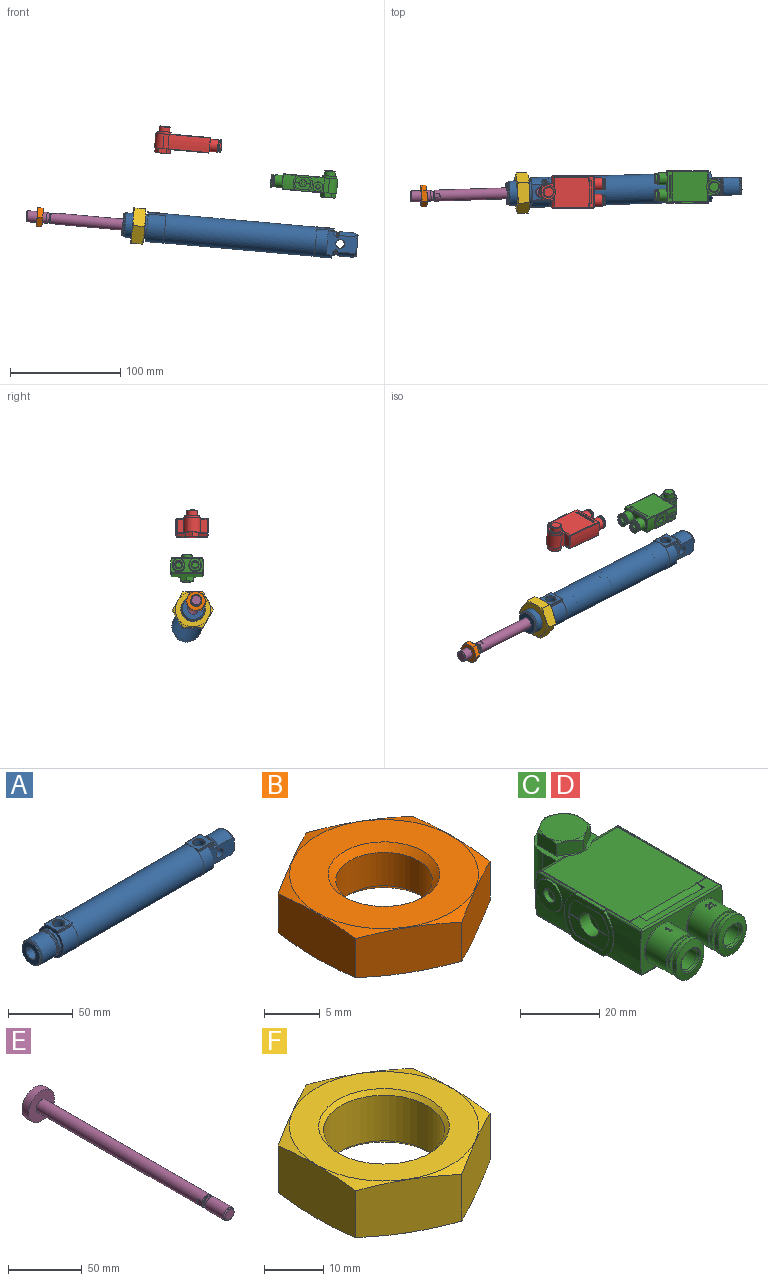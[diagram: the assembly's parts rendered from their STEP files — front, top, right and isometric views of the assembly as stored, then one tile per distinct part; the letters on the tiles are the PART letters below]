
ASSEMBLY  parts=6 mates=5
PART A: 96 faces, bbox 213.8x27.3x27.3 mm
  f0: cone r=866.03mm half-angle=60deg, axis (0,0,1), area 66.5mm2, adj f1
  f1: cylinder r=4.28mm len=21.42mm, axis (0,0,-1), area 576.4mm2, adj f0,f56
  f2: cone r=4.28mm half-angle=45deg, axis (0,0,1), area 23.6mm2, adj f3,f34
  f3: cylinder r=4.28mm len=10.34mm, axis (0,0,-1), area 278.2mm2, adj f2,f55
  f4: cylinder r=13.5mm len=27mm, axis (1,0,0), area 804.5mm2, adj f7,f21,f25,f52,f53,f66,f67,f68
  f5: cylinder r=4.28mm len=8.57mm, axis (0,0,-1), area 172.8mm2, adj f6,f55
  f6: plane 8.57x8.57mm, normal (0,0,1), area 57.6mm2, adj f5
  f7: plane 27.79x22.04mm, normal (0,-1,0), area 388.5mm2, adj f4,f8,f9,f10,f11,f12,f13,f60
  f8: torus R=10.65mm, axis (1,0,0), area 11.6mm2, adj f7,f67,f86,f88
  f9: torus R=10.65mm, axis (1,0,0), area 22.9mm2, adj f7,f67,f86,f91
  f10: cone r=11mm half-angle=45deg, axis (-1,0,0), area 25.8mm2, adj f7,f11,f64,f67
  f11: cylinder r=11mm len=16mm, axis (-1,0,0), area 267.8mm2, adj f7,f10,f67,f88
  f12: cylinder r=11mm len=16mm, axis (-1,0,0), area 267.8mm2, adj f7,f13,f65,f67
  f13: cone r=10.08mm half-angle=45deg, axis (1,0,0), area 23.6mm2, adj f7,f12,f67,f89
  f14: plane 3.86x0.71mm, normal (-1,0,0), area 2.5mm2, adj f16,f17,f69,f75
  f15: plane 3.86x0.71mm, normal (1,0,0), area 2.5mm2, adj f18,f20,f69,f75
  f16: plane 3.04x1.25mm, normal (0,0,1), area 2.8mm2, adj f14,f17
  f17: cone r=1.95mm half-angle=45deg, axis (0,0,-1), area 2.8mm2, adj f14,f16,f75
  f18: plane 3.04x1.25mm, normal (0,0,1), area 2.8mm2, adj f15,f20
  f19: cylinder r=0.4mm len=2.71mm, axis (1,0,0), area 1.5mm2, adj f21,f22,f49,f73
  f20: cone r=1.95mm half-angle=45deg, axis (0,0,-1), area 2.8mm2, adj f15,f18,f75
  f21: cylinder r=2.5mm len=6.7mm, axis (0,0,1), area 51.7mm2, adj f4,f19,f22,f49,f50,f51,f52,f53
  f22: plane 16x13.7mm, normal (0,0,1), area 144.5mm2, adj f19,f21,f23,f51,f56,f73,f94
  f23: cylinder r=0.4mm len=16mm, axis (1,0,0), area 10.1mm2, adj f22,f24,f73,f94
  f24: plane 16x1.55mm, normal (0,-1,0), area 24.8mm2, adj f23,f25,f73,f94
  f25: cylinder r=0.3mm len=16mm, axis (1,0,0), area 4.8mm2, adj f4,f24,f73,f94
  f26: cylinder r=13.25mm len=137.5mm, axis (-1,0,0), area 11447.2mm2, adj f73,f76
  f27: plane 3.9x0.6mm, normal (0,0,1), area 2.3mm2, adj f28,f30,f72
  f28: plane 3.86x0.71mm, normal (-1,0,0), area 2.5mm2, adj f27,f29,f30,f71
  f29: cone r=1.95mm half-angle=45deg, axis (0,0,-1), area 2.8mm2, adj f28,f30,f71
  f30: cylinder r=1.95mm len=3.9mm, axis (0,0,1), area 4mm2, adj f27,f28,f29,f31,f54,f72
  f31: plane 5x5mm, normal (0,0,1), area 7.7mm2, adj f30,f32
  f32: cylinder r=2.5mm len=6.7mm, axis (0,0,1), area 51.7mm2, adj f31,f33,f34,f78,f79,f80,f81,f82
  f33: cylinder r=0.4mm len=10.91mm, axis (1,0,0), area 6.7mm2, adj f32,f34,f77,f82
  f34: plane 16x13.7mm, normal (0,0,1), area 144.5mm2, adj f2,f32,f33,f35,f76,f77,f83
  f35: cylinder r=0.4mm len=16mm, axis (1,0,0), area 10.1mm2, adj f34,f36,f76,f77
  f36: plane 16x1.55mm, normal (0,-1,0), area 24.8mm2, adj f35,f37,f76,f77
  f37: cylinder r=0.3mm len=16mm, axis (1,0,0), area 4.8mm2, adj f36,f76,f77,f78
  f38: cylinder r=11mm len=22mm, axis (-1,0,0), area 138.2mm2, adj f39,f77
  f39: plane 22x22mm, normal (-1,0,0), area 23.8mm2, adj f38,f40
  f40: torus R=10.65mm, axis (1,0,0), area 80.1mm2, adj f39,f41
  f41: cylinder r=9.85mm len=19.7mm, axis (-1,0,0), area 47.6mm2, adj f40,f42
  f42: torus R=10.65mm, axis (1,0,0), area 39.2mm2, adj f41,f43
  f43: cone r=11mm half-angle=45deg, axis (-1,0,0), area 85.8mm2, adj f42,f44
  f44: cylinder r=11mm len=22mm, axis (-1,0,0), area 1033.3mm2, adj f43,f45
  f45: cone r=10mm half-angle=45deg, axis (1,0,0), area 93.3mm2, adj f44,f46
  f46: cylinder r=10mm len=20mm, axis (-1,0,0), area 50.3mm2, adj f45,f47
  f47: cone r=9.8mm half-angle=45deg, axis (1,0,0), area 17.6mm2, adj f46,f48
  f48: plane 19.6x19.6mm, normal (-1,0,0), area 223.2mm2, adj f47,f55
  f49: plane 2.12x1.55mm, normal (0,1,0), area 3.3mm2, adj f19,f21,f52,f73
  f50: plane 10.52x1.55mm, normal (0,1,0), area 16.3mm2, adj f21,f51,f53,f94
  f51: cylinder r=0.4mm len=11.11mm, axis (1,0,0), area 6.8mm2, adj f21,f22,f50,f94
  f52: cylinder r=0.3mm len=2.12mm, axis (1,0,0), area 0.6mm2, adj f4,f21,f49,f73
  f53: cylinder r=0.3mm len=10.52mm, axis (1,0,0), area 3.1mm2, adj f4,f21,f50,f94
  f54: cone r=1.95mm half-angle=45deg, axis (0,0,-1), area 2.8mm2, adj f30,f70,f72
  f55: cylinder r=5mm len=52.6mm, axis (-1,0,0), area 1522.1mm2, adj f3,f5,f48,f59
  f56: cone r=4.28mm half-angle=45deg, axis (0,0,1), area 23.6mm2, adj f1,f22
  f57: plane 25x25mm, normal (-1,0,0), area 490.9mm2, adj f58
  f58: cylinder r=12.5mm len=106.25mm, axis (-1,0,0), area 8344.9mm2, adj f57,f59
  f59: plane 25x25mm, normal (1,0,0), area 412.3mm2, adj f55,f58
  f60: cone r=10mm half-angle=45deg, axis (-1,0,0), area 5.3mm2, adj f7,f61,f63,f67
  f61: plane 19.6x16mm, normal (1,0,0), area 274mm2, adj f7,f60,f62,f67
  f62: cone r=10mm half-angle=45deg, axis (-1,0,0), area 5.3mm2, adj f7,f61,f64,f67
  f63: cylinder r=10mm len=16mm, axis (-1,0,0), area 14.8mm2, adj f7,f60,f65,f67
  f64: cylinder r=10mm len=16mm, axis (-1,0,0), area 14.8mm2, adj f7,f10,f62,f67
  f65: cone r=11mm half-angle=45deg, axis (-1,0,0), area 25.8mm2, adj f7,f12,f63,f67
  f66: plane 21.75x5.5mm, normal (1,0,0), area 83.7mm2, adj f4,f67
  f67: plane 27.79x22.04mm, normal (0,1,0), area 388.5mm2, adj f4,f8,f9,f10,f11,f12,f13,f60
  f68: plane 21.75x5.5mm, normal (1,0,0), area 83.7mm2, adj f4,f7
  f69: plane 3.9x0.6mm, normal (0,0,1), area 2.3mm2, adj f14,f15,f75
  f70: plane 3.04x1.25mm, normal (0,0,1), area 2.8mm2, adj f54,f72
  f71: plane 3.04x1.25mm, normal (0,0,1), area 2.8mm2, adj f28,f29
  f72: plane 3.86x0.71mm, normal (1,0,0), area 2.5mm2, adj f27,f30,f54,f70
  f73: plane 27x27mm, normal (-1,0,0), area 30.8mm2, adj f4,f19,f22,f23,f24,f25,f26,f49
  f74: plane 5x5mm, normal (0,0,1), area 7.7mm2, adj f21,f75
  f75: cylinder r=1.95mm len=3.9mm, axis (0,0,1), area 4mm2, adj f14,f15,f17,f20,f69,f74
  f76: plane 27x27mm, normal (1,0,0), area 30.8mm2, adj f26,f34,f35,f36,f37,f78,f80,f81
  f77: plane 27x27mm, normal (-1,0,0), area 202.2mm2, adj f33,f34,f35,f36,f37,f38,f78,f79
  f78: cylinder r=13.5mm len=27mm, axis (1,0,0), area 1082.7mm2, adj f32,f37,f76,f77,f79,f80
  f79: cylinder r=0.3mm len=10.32mm, axis (1,0,0), area 3mm2, adj f32,f77,f78,f82
  f80: cylinder r=0.3mm len=2.32mm, axis (1,0,0), area 0.7mm2, adj f32,f76,f78,f81
  f81: plane 2.32x1.55mm, normal (0,1,0), area 3.6mm2, adj f32,f76,f80,f83
  f82: plane 10.32x1.55mm, normal (0,1,0), area 16mm2, adj f32,f33,f77,f79
  f83: cylinder r=0.4mm len=2.91mm, axis (1,0,0), area 1.6mm2, adj f32,f34,f76,f81
  f84: cylinder r=4mm len=16mm, axis (0,-1,0), area 402.1mm2, adj f7,f67
  f85: torus R=10.65mm, axis (1,0,0), area 22.9mm2, adj f7,f67,f87,f90
  f86: cylinder r=9.85mm len=16mm, axis (-1,0,0), area 14.4mm2, adj f7,f8,f9,f67
  f87: cylinder r=9.85mm len=16mm, axis (-1,0,0), area 14.4mm2, adj f7,f67,f85,f89
  f88: cone r=10.08mm half-angle=45deg, axis (1,0,0), area 23.6mm2, adj f7,f8,f11,f67
  f89: torus R=10.65mm, axis (1,0,0), area 11.6mm2, adj f7,f13,f67,f87
  f90: plane 16x3.97mm, normal (1,0,0), area 6.3mm2, adj f7,f67,f85,f92
  f91: plane 16x3.97mm, normal (1,0,0), area 6.3mm2, adj f7,f9,f67,f93
  f92: cylinder r=11mm len=16mm, axis (-1,0,0), area 35.8mm2, adj f7,f67,f90,f94
  f93: cylinder r=11mm len=16mm, axis (-1,0,0), area 35.8mm2, adj f7,f67,f91,f95
  f94: plane 16x5.95mm, normal (1,0,0), area 53.5mm2, adj f4,f7,f22,f23,f24,f25,f50,f51
  f95: plane 16x5.95mm, normal (1,0,0), area 43.7mm2, adj f4,f7,f67,f93
PART B: 13 faces, bbox 19.6x19.6x5 mm
  f0: plane 9.82x4.98mm, normal (-1,0,0), area 46.4mm2, adj f1,f2,f4,f8
  f1: plane 8.5x4.98mm, normal (-0.5,0.87,0), area 46.4mm2, adj f0,f2,f8,f12
  f2: cone r=17.78mm half-angle=75deg, axis (0,0,1), area 26.9mm2, adj f0,f1,f3,f4,f5,f6,f12
  f3: plane 9.82x4.98mm, normal (1,0,0), area 46.4mm2, adj f2,f6,f8,f12
  f4: plane 8.5x4.98mm, normal (-0.5,-0.87,0), area 46.4mm2, adj f0,f2,f6,f8
  f5: plane 16.9x16.9mm, normal (0,0,-1), area 145.8mm2, adj f2,f9
  f6: plane 8.5x4.98mm, normal (0.5,-0.87,0), area 46.4mm2, adj f2,f3,f4,f8
  f7: plane 16.9x16.9mm, normal (0,0,1), area 145.8mm2, adj f8,f11
  f8: cone r=8.45mm half-angle=75deg, axis (0,0,-1), area 26.9mm2, adj f0,f1,f3,f4,f6,f7,f12
  f9: cone r=4.32mm half-angle=45deg, axis (0,0,-1), area 28mm2, adj f5,f10
  f10: cylinder r=4.32mm len=8.65mm, axis (0,0,1), area 99.1mm2, adj f9,f11
  f11: cone r=5mm half-angle=45deg, axis (0,0,1), area 28mm2, adj f7,f10
  f12: plane 8.5x4.98mm, normal (0.5,0.87,0), area 46.4mm2, adj f1,f2,f3,f8
PART C: 172 faces, bbox 30.2x60.9x25 mm
  f0: cylinder r=3.3mm len=6.6mm, axis (1,0,0), area 71.5mm2, adj f64,f137,f138,f139,f169
  f1: cylinder r=4.5mm len=9mm, axis (-1,0,0), area 8.7mm2, adj f2,f117
  f2: plane 9x9mm, normal (-1,0,0), area 51.7mm2, adj f1,f3
  f3: cylinder r=1.95mm len=3.9mm, axis (1,0,0), area 18.4mm2, adj f2,f4
  f4: plane 3.9x3.9mm, normal (-1,0,0), area 11.9mm2, adj f3
  f5: plane 0.52x0.28mm, normal (0,-1,0), area 0.1mm2, adj f6,f15,f16,f63
  f6: plane 0.51x0.24mm, normal (1,0,0), area 0.1mm2, adj f5,f7,f16,f63
  f7: plane 0.8x0.53mm, normal (0,1,0), area 0.4mm2, adj f6,f8,f16,f63
  f8: plane 0.51x0.24mm, normal (-1,0,0), area 0.1mm2, adj f7,f9,f16,f63
  f9: plane 0.52x0.28mm, normal (0,-1,0), area 0.1mm2, adj f8,f10,f16,f63
  f10: plane 1.68x0.52mm, normal (-1,0,0), area 0.9mm2, adj f9,f11,f16,f63
  f11: plane 0.53x0.24mm, normal (0,-1,0), area 0.1mm2, adj f10,f12,f16,f63
  f12: plane 0.52x0.4mm, normal (0.82,-0.57,0), area 0.3mm2, adj f11,f13,f16,f63
  f13: plane 0.51x0.34mm, normal (1,0,0), area 0.2mm2, adj f12,f14,f16,f63
  f14: plane 0.52x0.4mm, normal (-0.82,0.57,0), area 0.3mm2, adj f13,f15,f16,f63
  f15: plane 1.34x0.52mm, normal (1,0,0), area 0.7mm2, adj f5,f14,f16,f63
  f16: plane 1.92x0.8mm, normal (0,0,1), area 0.7mm2, adj f5,f6,f7,f8,f9,f10,f11,f12
  f17: plane 0.52x0.28mm, normal (0,-1,0), area 0.1mm2, adj f18,f27,f28,f32
  f18: plane 0.52x0.24mm, normal (1,0,0), area 0.1mm2, adj f17,f19,f28,f32
  f19: plane 0.8x0.52mm, normal (0,1,0), area 0.4mm2, adj f18,f20,f28,f32
  f20: plane 0.41x0.24mm, normal (-1,0,0), area 0.1mm2, adj f19,f21,f28,f32
  f21: plane 0.46x0.28mm, normal (0,-1,0), area 0.1mm2, adj f20,f22,f28,f32
  f22: plane 1.68x0.46mm, normal (-1,0,0), area 0.8mm2, adj f21,f23,f28,f32
  f23: plane 0.49x0.24mm, normal (0,-1,0), area 0.1mm2, adj f22,f24,f28,f32
  f24: plane 0.52x0.4mm, normal (0.82,-0.57,0), area 0.2mm2, adj f23,f25,f28,f32
  f25: plane 0.52x0.34mm, normal (1,0,0), area 0.2mm2, adj f24,f26,f28,f32
  f26: plane 0.52x0.4mm, normal (-0.82,0.57,0), area 0.2mm2, adj f25,f27,f28,f32
  f27: plane 1.34x0.49mm, normal (1,0,0), area 0.7mm2, adj f17,f26,f28,f32
  f28: plane 1.92x0.8mm, normal (0,0,1), area 0.7mm2, adj f17,f18,f19,f20,f21,f22,f23,f24
  f29: cylinder r=0.58mm len=1.16mm, axis (0,0,1), area 1mm2, adj f30,f32,f61,f62
  f30: plane 0.43x0.24mm, normal (0,1,0), area 0.1mm2, adj f29,f31,f32,f62
  f31: cylinder r=0.34mm len=0.68mm, axis (0,0,1), area 0.6mm2, adj f30,f32,f56,f62
  f32: cylinder r=5.53mm len=11.05mm, axis (0,1,0), area 251.7mm2, adj f17,f18,f19,f20,f21,f22,f23,f24
  f33: plane 11.05x11.05mm, normal (0,-1,0), area 17.4mm2, adj f32,f34
  f34: cylinder r=5mm len=10mm, axis (0,1,0), area 25.1mm2, adj f33,f35
  f35: plane 10x10mm, normal (0,-1,0), area 40.1mm2, adj f34,f36
  f36: cylinder r=3.5mm len=7mm, axis (0,1,0), area 22mm2, adj f35,f37
  f37: plane 11.8x9.8mm, normal (0,1,0), area 56.5mm2, adj f36,f39,f72,f73,f100
  f38: cone r=3.58mm half-angle=80deg, axis (0,1,0), area 55.9mm2, adj f39,f72,f73,f98,f100
  f39: cylinder r=4.9mm len=9.8mm, axis (0,1,0), area 19.2mm2, adj f37,f38,f72,f100
  f40: plane 17.5x14.1mm, normal (-1,0,0), area 77.5mm2, adj f41,f42,f43,f104,f105,f106,f120,f129
  f41: plane 9.26x0.15mm, normal (0,0,-1), area 1.4mm2, adj f40,f42,f104,f138
  f42: cylinder r=7.15mm len=10.9mm, axis (-1,0,0), area 1.9mm2, adj f40,f41,f105,f137,f138,f139
  f43: cylinder r=8.75mm len=14.1mm, axis (-1,0,0), area 6.2mm2, adj f40,f44,f117,f118,f120,f129
  f44: cylinder r=0.5mm len=13.74mm, axis (0,-1,0), area 9.3mm2, adj f43,f45,f117,f129
  f45: cylinder r=1.2mm len=1.2mm, axis (1,0,0), area 0.8mm2, adj f44,f82,f117,f123,f129
  f46: cylinder r=6.6mm len=13.21mm, axis (0,0,1), area 81mm2, adj f79,f129,f135,f136,f158
  f47: plane 6.57x4.77mm, normal (0.5,0.87,0), area 27.8mm2, adj f48,f159,f162,f164,f168
  f48: plane 7.5x4.77mm, normal (1,0,0), area 27.8mm2, adj f47,f159,f163,f164,f165
  f49: plane 7.5x4.77mm, normal (-1,0,0), area 27.8mm2, adj f74,f159,f166,f167,f168
  f50: plane 4x1.44mm, normal (0,1,0), area 5.8mm2, adj f51,f55,f169,f170
  f51: plane 4x1.25mm, normal (0,0.5,0.87), area 5.8mm2, adj f50,f52,f169,f170
  f52: plane 4x1.25mm, normal (0,-0.5,0.87), area 5.8mm2, adj f51,f53,f169,f170
  f53: plane 4x1.44mm, normal (0,-1,0), area 5.8mm2, adj f52,f54,f169,f170
  f54: plane 4x1.25mm, normal (0,-0.5,-0.87), area 5.8mm2, adj f53,f55,f169,f170
  f55: plane 4x1.25mm, normal (0,0.5,-0.87), area 5.8mm2, adj f50,f54,f169,f170
  f56: plane 0.82x0.77mm, normal (0.68,-0.73,0), area 0.5mm2, adj f31,f32,f57,f62
  f57: plane 0.37x0.33mm, normal (1,0,0), area 0.1mm2, adj f32,f56,f58,f62
  f58: plane 1.16x0.52mm, normal (0,1,0), area 0.5mm2, adj f32,f57,f59,f62
  f59: plane 0.52x0.24mm, normal (-1,0,0), area 0.1mm2, adj f32,f58,f60,f62
  f60: plane 0.9x0.52mm, normal (0,-1,0), area 0.4mm2, adj f32,f59,f61,f62
  f61: plane 0.72x0.68mm, normal (-0.68,0.73,0), area 0.5mm2, adj f29,f32,f60,f62
  f62: plane 1.92x1.16mm, normal (0,0,1), area 1mm2, adj f29,f30,f31,f56,f57,f58,f59,f60
  f63: cylinder r=5.53mm len=11.05mm, axis (0,-1,0), area 252.7mm2, adj f5,f6,f7,f8,f9,f10,f11,f12
  f64: cylinder r=45mm len=3.85mm, axis (0,-1,0), area 1mm2, adj f0,f104,f137,f138
  f65: torus R=5.72mm, axis (0,1,0), area 11mm2, adj f63,f119
  f66: cone r=3.23mm half-angle=10deg, axis (0,-1,0), area 15.2mm2, adj f67,f101
  f67: torus R=3.53mm, axis (0,1,0), area 10mm2, adj f66,f68
  f68: cone r=5.9mm half-angle=80deg, axis (0,1,0), area 55.8mm2, adj f67,f69,f70,f71,f103
  f69: cylinder r=4.9mm len=9.8mm, axis (0,1,0), area 19.2mm2, adj f68,f70,f103,f127
  f70: plane 2.21x1.47mm, normal (1,0,0), area 2.5mm2, adj f68,f69,f71,f127
  f71: cylinder r=4.9mm len=9.8mm, axis (0,1,0), area 19.2mm2, adj f68,f70,f103,f127
  f72: plane 2.21x1.47mm, normal (-1,0,0), area 2.5mm2, adj f37,f38,f39,f73
  f73: cylinder r=4.9mm len=9.8mm, axis (0,1,0), area 19.2mm2, adj f37,f38,f72,f100
  f74: plane 6.57x4.77mm, normal (-0.5,-0.87,0), area 27.8mm2, adj f49,f159,f161,f163,f166
  f75: cylinder r=7.2mm len=10.54mm, axis (0,0,1), area 4.2mm2, adj f120,f133,f134,f159
  f76: plane 8.57x8.57mm, normal (0,0,-1), area 57.6mm2, adj f77
  f77: cone r=4.86mm half-angle=45deg, axis (0,0,1), area 23.6mm2, adj f76,f78
  f78: cylinder r=4.86mm len=9.73mm, axis (0,0,1), area 131.4mm2, adj f77,f79
  f79: plane 13.21x13.21mm, normal (0,0,-1), area 62.7mm2, adj f46,f78
  f80: cylinder r=45mm len=37.4mm, axis (0,-1,0), area 497.1mm2, adj f81,f114,f115,f116,f119,f121,f122,f130
  f81: cylinder r=0.5mm len=28.54mm, axis (1,0,0), area 22.1mm2, adj f80,f115,f119,f120,f125,f126
  f82: plane 32.63x14.1mm, normal (1,0,0), area 30.8mm2, adj f45,f83,f120,f123,f128,f129,f140,f147
  f83: plane 13.3x0.23mm, normal (0,1,0), area 3.1mm2, adj f82,f84,f147,f154
  f84: plane 32.4x14.1mm, normal (-1,0,0), area 30.6mm2, adj f83,f120,f129,f132,f134,f135,f143,f147
  f85: plane 32.4x14.1mm, normal (1,0,0), area 30.6mm2, adj f86,f120,f129,f131,f133,f136,f141,f144
  f86: plane 13.3x0.23mm, normal (0,1,0), area 3.1mm2, adj f85,f87,f141,f171
  f87: plane 32.63x14.1mm, normal (-1,0,0), area 30.8mm2, adj f86,f120,f121,f122,f129,f130,f141,f146
  f88: cylinder r=1.9mm len=20.57mm, axis (1,0,0), area 61.4mm2, adj f89,f94,f95,f129
  f89: plane 20.57x0.6mm, normal (0,0,-1), area 12.3mm2, adj f88,f90,f94,f95
  f90: plane 20.57x1.9mm, normal (0,1,0), area 39.1mm2, adj f89,f94,f95,f129
  f91: plane 20.57x1.9mm, normal (0,1,0), area 39.1mm2, adj f92,f112,f113,f120
  f92: plane 20.57x0.6mm, normal (0,0,1), area 12.3mm2, adj f91,f93,f112,f113
  f93: cylinder r=1.9mm len=20.57mm, axis (1,0,0), area 61.4mm2, adj f92,f112,f113,f120
  f94: plane 2.5x1.9mm, normal (1,0,0), area 1.9mm2, adj f88,f89,f90,f129
  f95: plane 2.5x1.9mm, normal (-1,0,0), area 1.9mm2, adj f88,f89,f90,f129
  f96: cylinder r=3.1mm len=10.9mm, axis (0,1,0), area 212.3mm2, adj f97,f99
  f97: cone r=3.1mm half-angle=10deg, axis (0,-1,0), area 15.2mm2, adj f96,f98
  f98: torus R=3.53mm, axis (0,-1,0), area 10mm2, adj f38,f97
  f99: plane 6.2x6.2mm, normal (0,-1,0), area 30.2mm2, adj f96
  f100: plane 2.21x1.47mm, normal (1,0,0), area 2.5mm2, adj f37,f38,f39,f73
  f101: cylinder r=3.1mm len=10.9mm, axis (0,-1,0), area 212.3mm2, adj f66,f102
  f102: plane 6.2x6.2mm, normal (0,-1,0), area 30.2mm2, adj f101
  f103: plane 2.05x1.32mm, normal (-1,0,0), area 2.5mm2, adj f68,f69,f71,f127
  f104: cylinder r=7.15mm len=10.9mm, axis (-1,0,0), area 1.9mm2, adj f40,f41,f64,f105,f137,f138
  f105: plane 9.26x0.15mm, normal (0,0,1), area 1.4mm2, adj f40,f42,f104,f137
  f106: cylinder r=8.75mm len=14.1mm, axis (-1,0,0), area 6.2mm2, adj f40,f120,f124,f125,f126,f129
  f107: cylinder r=3.5mm len=7mm, axis (0,-1,0), area 22mm2, adj f108,f127
  f108: plane 10x10mm, normal (0,-1,0), area 40.1mm2, adj f107,f109
  f109: cylinder r=5mm len=10mm, axis (0,-1,0), area 25.1mm2, adj f108,f110
  f110: plane 11.05x11.05mm, normal (0,-1,0), area 17.4mm2, adj f63,f109
  f111: torus R=5.72mm, axis (0,-1,0), area 11mm2, adj f32,f119
  f112: plane 2.5x1.9mm, normal (1,0,0), area 1.9mm2, adj f91,f92,f93,f120
  f113: plane 2.5x1.9mm, normal (-1,0,0), area 1.9mm2, adj f91,f92,f93,f120
  f114: cylinder r=0.5mm len=28.54mm, axis (1,0,0), area 22.1mm2, adj f80,f116,f119,f124,f125,f129
  f115: cylinder r=0.5mm len=37.11mm, axis (0,-1,0), area 25.9mm2, adj f80,f81,f120,f121
  f116: cylinder r=0.5mm len=37.11mm, axis (0,-1,0), area 25.9mm2, adj f80,f114,f129,f130
  f117: cylinder r=45mm len=13.48mm, axis (0,-1,0), area 87.3mm2, adj f1,f43,f44,f45,f118,f123,f128
  f118: cylinder r=0.5mm len=13.73mm, axis (0,-1,0), area 9.3mm2, adj f43,f117,f120,f128
  f119: plane 29.5x13.1mm, normal (0,-1,0), area 176.3mm2, adj f65,f80,f81,f111,f114,f125
  f120: plane 35.7x28.67mm, normal (0,0,1), area 918.9mm2, adj f40,f43,f75,f81,f82,f84,f85,f87
  f121: cylinder r=1.2mm len=1.2mm, axis (1,0,0), area 0.8mm2, adj f80,f87,f115,f120,f122
  f122: plane 11.7x1.02mm, normal (0,1,0), area 10.4mm2, adj f80,f87,f121,f130
  f123: plane 11.7x1.02mm, normal (0,1,0), area 10.4mm2, adj f45,f82,f117,f128
  f124: cylinder r=0.5mm len=13.01mm, axis (0,-1,0), area 8.9mm2, adj f106,f114,f125,f129
  f125: cylinder r=45mm len=13.25mm, axis (0,-1,0), area 138mm2, adj f81,f106,f114,f119,f124,f126
  f126: cylinder r=0.5mm len=13.01mm, axis (0,-1,0), area 8.9mm2, adj f81,f106,f120,f125
  f127: plane 11.8x9.8mm, normal (0,1,0), area 56.5mm2, adj f69,f70,f71,f103,f107
  f128: cylinder r=1.2mm len=1.2mm, axis (1,0,0), area 0.8mm2, adj f82,f117,f118,f120,f123
  f129: plane 35.7x28.67mm, normal (0,0,-1), area 923.6mm2, adj f40,f43,f44,f45,f46,f82,f84,f85
  f130: cylinder r=1.2mm len=1.2mm, axis (1,0,0), area 0.8mm2, adj f80,f87,f116,f122,f129
  f131: plane 11.7x6mm, normal (0,1,0), area 70.2mm2, adj f85,f133,f136,f157
  f132: plane 11.7x6mm, normal (0,1,0), area 70.2mm2, adj f84,f134,f135,f156
  f133: cylinder r=1.2mm len=9.23mm, axis (1,0,0), area 14.1mm2, adj f75,f85,f120,f131,f157,f159
  f134: cylinder r=1.2mm len=9.23mm, axis (1,0,0), area 14.1mm2, adj f75,f84,f120,f132,f156,f159
  f135: cylinder r=1.2mm len=10.34mm, axis (1,0,0), area 15.1mm2, adj f46,f84,f129,f132,f156,f158
  f136: cylinder r=1.2mm len=10.34mm, axis (1,0,0), area 15.1mm2, adj f46,f85,f129,f131,f157,f158
  f137: plane 14.3x5.32mm, normal (-1,0,0), area 51.4mm2, adj f0,f42,f64,f104,f105,f139
  f138: plane 14.3x5.32mm, normal (-1,0,0), area 51.4mm2, adj f0,f41,f42,f64,f104,f139
  f139: cylinder r=45mm len=3.85mm, axis (0,-1,0), area 1mm2, adj f0,f42,f137,f138
  f140: plane 3.68x0.4mm, normal (0,1,0), area 1.5mm2, adj f82,f120,f142,f147
  f141: plane 32.23x3.68mm, normal (0,0,1), area 8.3mm2, adj f85,f86,f87,f144,f145,f146
  f142: plane 0.4x0.23mm, normal (-1,0,0), area 0.1mm2, adj f120,f140,f143,f147
  f143: plane 3.45x0.4mm, normal (0,-1,0), area 1.4mm2, adj f84,f120,f142,f147
  f144: plane 3.45x0.4mm, normal (0,-1,0), area 1.4mm2, adj f85,f120,f141,f145
  f145: plane 0.4x0.23mm, normal (1,0,0), area 0.1mm2, adj f120,f141,f144,f146
  f146: plane 3.68x0.4mm, normal (0,1,0), area 1.5mm2, adj f87,f120,f141,f145
  f147: plane 32.23x3.68mm, normal (0,0,1), area 8.3mm2, adj f82,f83,f84,f140,f142,f143
  f148: plane 3.68x0.4mm, normal (0,1,0), area 1.5mm2, adj f82,f129,f149,f154
  f149: plane 0.4x0.23mm, normal (-1,0,0), area 0.1mm2, adj f129,f148,f150,f154
  f150: plane 3.45x0.4mm, normal (0,-1,0), area 1.4mm2, adj f84,f129,f149,f154
  f151: plane 3.45x0.4mm, normal (0,-1,0), area 1.4mm2, adj f85,f129,f152,f171
  f152: plane 0.4x0.23mm, normal (1,0,0), area 0.1mm2, adj f129,f151,f153,f171
  f153: plane 3.68x0.4mm, normal (0,1,0), area 1.5mm2, adj f87,f129,f152,f171
  f154: plane 32.23x3.68mm, normal (0,0,-1), area 8.3mm2, adj f82,f83,f84,f148,f149,f150
  f155: cylinder r=7.5mm len=15mm, axis (0,0,1), area 313.4mm2, adj f156,f157,f158,f159
  f156: plane 13.3x4.91mm, normal (-1,0,0), area 61.3mm2, adj f132,f134,f135,f155,f158,f159
  f157: plane 13.3x4.91mm, normal (1,0,0), area 61.3mm2, adj f131,f133,f136,f155,f158,f159
  f158: plane 15x12.41mm, normal (0,0,-1), area 35.2mm2, adj f46,f135,f136,f155,f156,f157
  f159: plane 15x14.7mm, normal (0,0,1), area 54mm2, adj f47,f48,f49,f74,f75,f133,f134,f155
  f160: plane 12x12mm, normal (0,0,1), area 113.1mm2, adj f161,f162,f164,f165,f166,f167
  f161: cone r=6mm half-angle=60deg, axis (0,0,-1), area 3.5mm2, adj f74,f160,f163
  f162: cone r=6mm half-angle=60deg, axis (0,0,-1), area 3.5mm2, adj f47,f160,f168
  f163: plane 6.57x4.77mm, normal (0.5,-0.87,0), area 27.8mm2, adj f48,f74,f159,f161,f165
  f164: cone r=6mm half-angle=60deg, axis (0,0,-1), area 3.5mm2, adj f47,f48,f160
  f165: cone r=6mm half-angle=60deg, axis (0,0,-1), area 3.5mm2, adj f48,f160,f163
  f166: cone r=6mm half-angle=60deg, axis (0,0,-1), area 3.5mm2, adj f49,f74,f160
  f167: cone r=6mm half-angle=60deg, axis (0,0,-1), area 3.5mm2, adj f49,f160,f168
  f168: plane 6.57x4.77mm, normal (-0.5,0.87,0), area 27.8mm2, adj f47,f49,f159,f162,f167
  f169: plane 6.6x6.6mm, normal (-1,0,0), area 28.8mm2, adj f0,f50,f51,f52,f53,f54,f55
  f170: plane 2.89x2.5mm, normal (-1,0,0), area 5.4mm2, adj f50,f51,f52,f53,f54,f55
  f171: plane 32.23x3.68mm, normal (0,0,-1), area 8.3mm2, adj f85,f86,f87,f151,f152,f153
PART D: same geometry as C
PART E: 17 faces, bbox 25.2x187x25.2 mm
  f0: plane 4.58x4.36mm, normal (1,0,0), area 19.8mm2, adj f3,f4,f5,f15,f16
  f1: plane 4.78x4.55mm, normal (-1,0,0), area 19.8mm2, adj f2,f3,f4,f5,f15
  f2: plane 4.36x0.5mm, normal (0,-1,0), area 1.5mm2, adj f1,f15
  f3: plane 9x3.33mm, normal (0,-1,0), area 2.3mm2, adj f0,f1,f5,f15
  f4: plane 9x3.33mm, normal (0,-1,0), area 2.3mm2, adj f0,f1,f5,f15
  f5: torus R=4.8mm, axis (0,1,0), area 24.9mm2, adj f0,f1,f3,f4,f6
  f6: cylinder r=4.2mm len=8.4mm, axis (0,-1,0), area 21mm2, adj f5,f7
  f7: torus R=4.8mm, axis (0,1,0), area 5.5mm2, adj f6,f8
  f8: cone r=5mm half-angle=20deg, axis (0,-1,0), area 64.8mm2, adj f7,f9
  f9: cylinder r=5mm len=17.54mm, axis (0,-1,0), area 550.9mm2, adj f8,f10
  f10: cone r=4.23mm half-angle=45deg, axis (0,1,0), area 31.5mm2, adj f9,f11
  f11: plane 8.47x8.47mm, normal (0,-1,0), area 56.3mm2, adj f10
  f12: plane 25x25mm, normal (0,1,0), area 490.9mm2, adj f13
  f13: cylinder r=12.5mm len=25mm, axis (0,-1,0), area 490.9mm2, adj f12,f14
  f14: plane 25x25mm, normal (0,-1,0), area 412.3mm2, adj f13,f15
  f15: cylinder r=5mm len=158.6mm, axis (0,-1,0), area 4942mm2, adj f0,f1,f2,f3,f4,f14,f16
  f16: plane 4.36x0.5mm, normal (0,-1,0), area 1.5mm2, adj f0,f15
PART F: 13 faces, bbox 37x37x11 mm
  f0: plane 18.48x10.97mm, normal (-1,0,0), area 194.2mm2, adj f1,f2,f4,f8
  f1: plane 16x10.97mm, normal (-0.5,0.87,0), area 194.2mm2, adj f0,f2,f8,f12
  f2: cone r=36.48mm half-angle=75deg, axis (0,0,1), area 90.7mm2, adj f0,f1,f3,f4,f5,f6,f12
  f3: plane 18.48x10.97mm, normal (1,0,0), area 194.3mm2, adj f2,f6,f8,f12
  f4: plane 16x10.97mm, normal (-0.5,-0.87,0), area 194.2mm2, adj f0,f2,f6,f8
  f5: plane 31.9x31.9mm, normal (0,0,-1), area 419.1mm2, adj f2,f9
  f6: plane 16x10.97mm, normal (0.5,-0.87,0), area 194.3mm2, adj f2,f3,f4,f8
  f7: plane 31.9x31.9mm, normal (0,0,1), area 419.1mm2, adj f8,f11
  f8: cone r=15.95mm half-angle=75deg, axis (0,0,-1), area 90.7mm2, adj f0,f1,f3,f4,f6,f7,f12
  f9: cone r=10.19mm half-angle=45deg, axis (0,0,-1), area 76.4mm2, adj f5,f10
  f10: cylinder r=10.19mm len=20.38mm, axis (0,0,1), area 600.2mm2, adj f9,f11
  f11: cone r=11mm half-angle=45deg, axis (0,0,1), area 76.4mm2, adj f7,f10
  f12: plane 16x10.97mm, normal (0.5,0.87,0), area 194.2mm2, adj f1,f2,f3,f8
PLACE A rot(axis=(0.01,0.94,0.34),5.4deg) t=(-75.95,46.07,43.69)mm
PLACE B rot(axis=(0.02,-1,0.02),85deg) t=(-153.75,43.58,50.58)mm
PLACE C rot(axis=(-0.71,-0.71,0.03),176.4deg) t=(106.53,51.9,79.48)mm
PLACE D rot(axis=(0.71,-0.71,-0.03),176.4deg) t=(-34.36,47.03,118.93)mm
PLACE E rot(axis=(-0.61,-0.57,-0.55),116deg) t=(-135.37,44.16,48.95)mm
PLACE F rot(axis=(0.02,-1,0.02),85deg) t=(-67.32,46.34,42.92)mm
MATE cylindrical D.f75 <-> A.f2  axis (-0.09,0,-1) through (-39.9,47.03,108.53)mm
MATE fastened B.f2 <-> E.f5  axis (-1,-0.03,0.09) through (-153.75,43.58,50.58)mm
MATE slider E.f5 <-> A.f8  axis (-1,-0.03,0.09) through (-62.39,46.5,42.49)mm
MATE cylindrical C.f75 <-> A.f0  axis (-0.09,0,-1) through (110.16,51.9,68.27)mm
MATE fastened F.f2 <-> A.f8  axis (-1,-0.03,0.09) through (-66.51,46.37,42.85)mm
